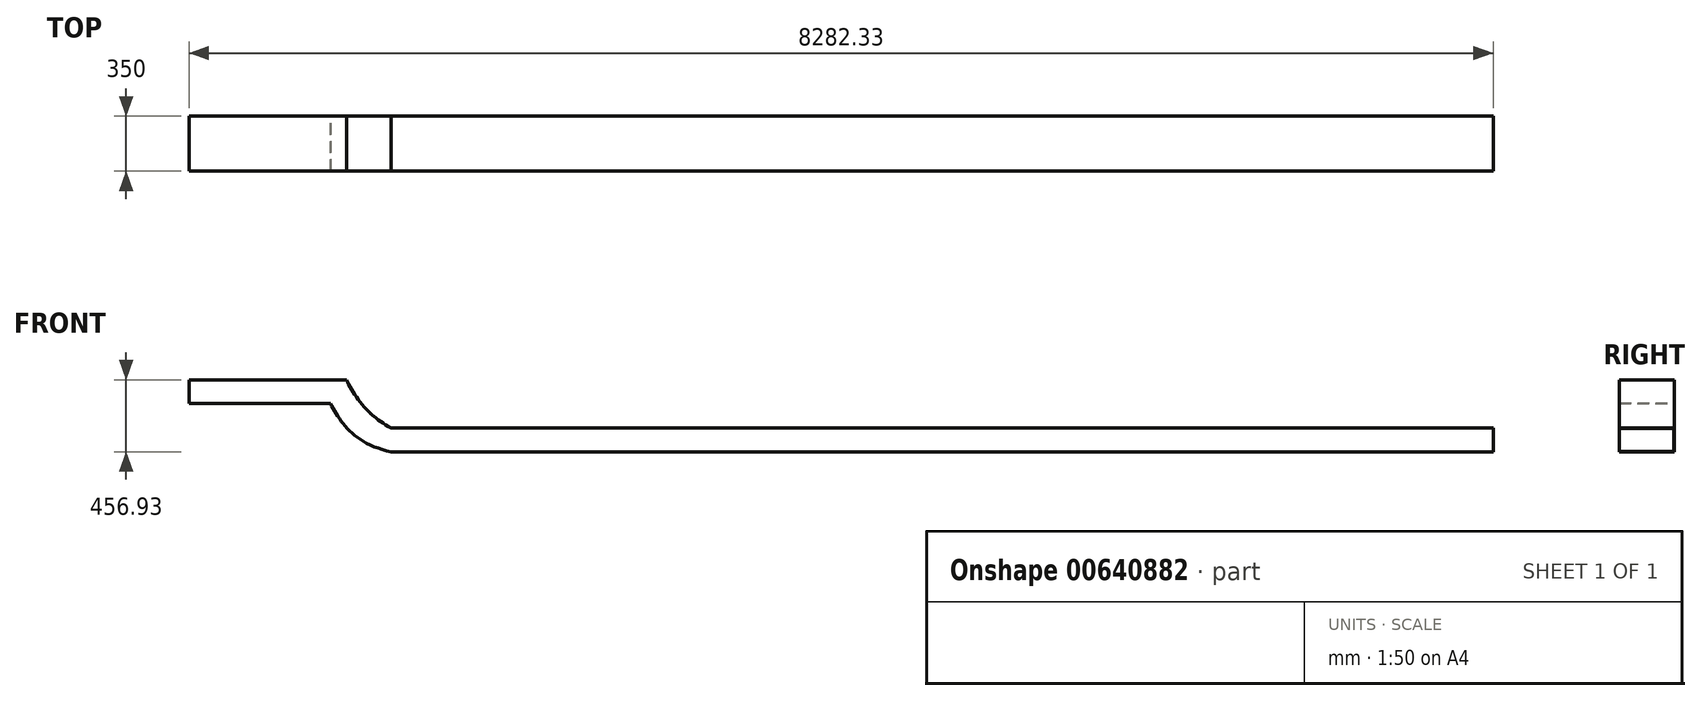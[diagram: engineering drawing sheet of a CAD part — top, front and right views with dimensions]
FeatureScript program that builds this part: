
annotation { "Feature Type Name" : "Feature", "Feature Type Description" : "" }
export const myFeature = defineFeature(function(context is Context, id is Id, definition is map)
    precondition{}
    {
        {
            var Q0;
            Q0=qCreatedBy(makeId("Front.planeOp"),FACE);
            var sketch = newSketch(context, id + "F0", { "sketchPlane" : qUnion([Q0])});
            skLineSegment(sketch, "E0", {"start": v(-1395.37, 456.93) * mm, "end": v(-395.37, 456.93) * mm});
            skLineSegment(sketch, "E1", {"start": v(-113.04, 150) * mm, "end": v(6886.96, 150) * mm});
            skLineSegment(sketch, "E2", {"start": v(-1395.37, 456.93) * mm, "end": v(-1395.37, 306.93) * mm});
            skFitSpline(sketch, "E3", {"points": [v(-395.37, 456.93) * mm, v(-276.91, 277.02) * mm, v(-113.04, 150) * mm], "startDerivative": vector(124.12, -317.85) * mm, "endDerivative": vector(435.87, -259.93) * mm});
            skLineSegment(sketch, "E4", {"start": v(-1395.37, 306.93) * mm, "end": v(-496.95, 306.93) * mm});
            skFitSpline(sketch, "E5", {"points": [v(-496.95, 306.93) * mm, v(-113.04, 0) * mm], "startDerivative": vector(178.85, -365.87) * mm, "endDerivative": vector(688.93, -140.3) * mm});
            skLineSegment(sketch, "E6", {"start": v(-113.04, 0) * mm, "end": v(6886.96, 0) * mm});
            skLineSegment(sketch, "E7", {"start": v(6886.96, 0) * mm, "end": v(6886.96, 150) * mm});
            skSolve(sketch);
        }
        {
            var Q0;
            Q0=makeQuery(id+"F0.imprint","IMPRINT",FACE,{"disambiguationData":[TD([[makeQuery(id+"F0.imprint","IMPRINT",EDGE,{"derivedFrom":sQuery(id+"F0.wireOp",EDGE,"E0")}),-1.0]])]});
            extrude(context, id + "F1", {"entities" : qUnion([Q0]), "depth" : 350 * mm, "offsetDistance" : 25.4 * mm});
        }
        {
            var Q0;
            Q0=makeQuery(id+"F1.opExtrude","SWEPT_FACE",FACE,{"disambiguationData":[OSD([sQuery(id+"F0.wireOp",EDGE,"E2")])]});
            var Q1;
            Q1=makeQuery(id+"F1.opExtrude","SWEPT_FACE",FACE,{"disambiguationData":[OSD([sQuery(id+"F0.wireOp",EDGE,"E7")])]});
            shell(context, id + "F2", {"entities" : qUnion([Q0, Q1]), "thickness" : 2.54 * mm});
        }
    });
